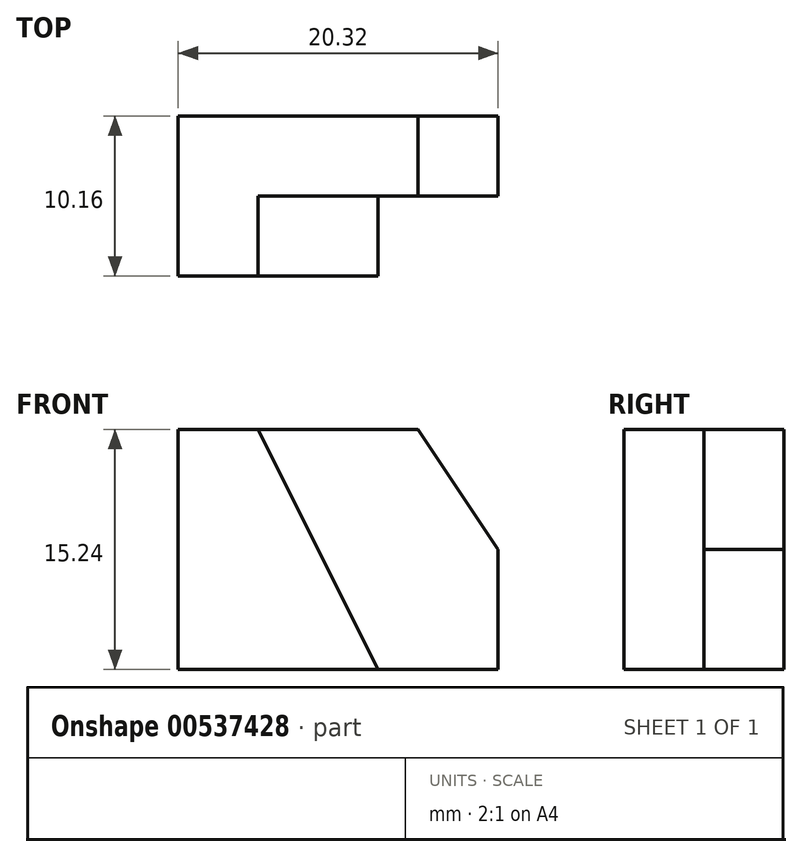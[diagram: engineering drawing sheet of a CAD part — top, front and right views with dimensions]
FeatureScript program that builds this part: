
annotation { "Feature Type Name" : "Feature", "Feature Type Description" : "" }
export const myFeature = defineFeature(function(context is Context, id is Id, definition is map)
    precondition{}
    {
        {
            var Q0;
            Q0=qCreatedBy(makeId("Front.planeOp"),FACE);
            var sketch = newSketch(context, id + "F0", { "sketchPlane" : qUnion([Q0])});
            skLineSegment(sketch, "E0", {"start": v(0, 0) * mm, "end": v(12.7, 0) * mm});
            skLineSegment(sketch, "E1", {"start": v(0, 0) * mm, "end": v(0, 15.24) * mm});
            skLineSegment(sketch, "E2", {"start": v(0, 15.24) * mm, "end": v(5.08, 15.24) * mm});
            skLineSegment(sketch, "E3", {"start": v(5.08, 15.24) * mm, "end": v(12.7, 0) * mm});
            skSolve(sketch);
        }
        {
            var Q0;
            Q0 = qSketchRegion(id + "F0", true);
            extrude(context, id + "F1", {"entities" : qUnion([Q0]), "depth" : 5.08 * mm, "offsetDistance" : 25.4 * mm});
        }
        {
            var Q0;
            Q0=makeQuery(id+"F1.opExtrude","CAP_FACE",FACE,{"disambiguationData":[OSD([sQuery(id+"F0.wireOp",EDGE,"E0"),sQuery(id+"F0.wireOp",EDGE,"E1"),sQuery(id+"F0.wireOp",EDGE,"E2"),sQuery(id+"F0.wireOp",EDGE,"E3")])],"isStart":true});
            var sketch = newSketch(context, id + "F2", { "sketchPlane" : qUnion([Q0])});
            skLineSegment(sketch, "E4", {"start": v(0, 0) * mm, "end": v(-20.32, 0) * mm});
            skLineSegment(sketch, "E5", {"start": v(-20.32, 0) * mm, "end": v(-20.32, 7.62) * mm});
            skLineSegment(sketch, "E6", {"start": v(0, 15.24) * mm, "end": v(-15.24, 15.24) * mm});
            skLineSegment(sketch, "E7", {"start": v(-15.24, 15.24) * mm, "end": v(-20.32, 7.62) * mm});
            skSolve(sketch);
        }
        {
            var Q0;
            Q0 = qSketchRegion(id + "F2", true);
            var Q1;
            {var subQ1=makeQuery(id+"F1.opExtrude","CAP_EDGE",EDGE,{"disambiguationData":[OSD([sQuery(id+"F0.wireOp",EDGE,"E1")])],"isStart":true});Q1=makeQuery(id+"F2.imprint","IMPRINT",FACE,{"disambiguationData":[TD([[makeQuery(id+"F2.imprint","IMPRINT",EDGE,{"derivedFrom":subQ1}),1.0]])]});}
            var Q2;
            {var subQ3=sQuery(id+"F2.wireOp",EDGE,"E5");Q2=makeQuery(id+"F2.imprint","IMPRINT",FACE,{"disambiguationData":[TD([[makeQuery(id+"F2.imprint","IMPRINT",EDGE,{"derivedFrom":subQ3}),-1.0]])]});}
            extrude(context, id + "F3", {"entities" : qUnion([Q0, Q1, Q2]), "operationType" : NewBodyOperationType.ADD, "depth" : 5.08 * mm, "offsetDistance" : 25.4 * mm});
        }
    });
